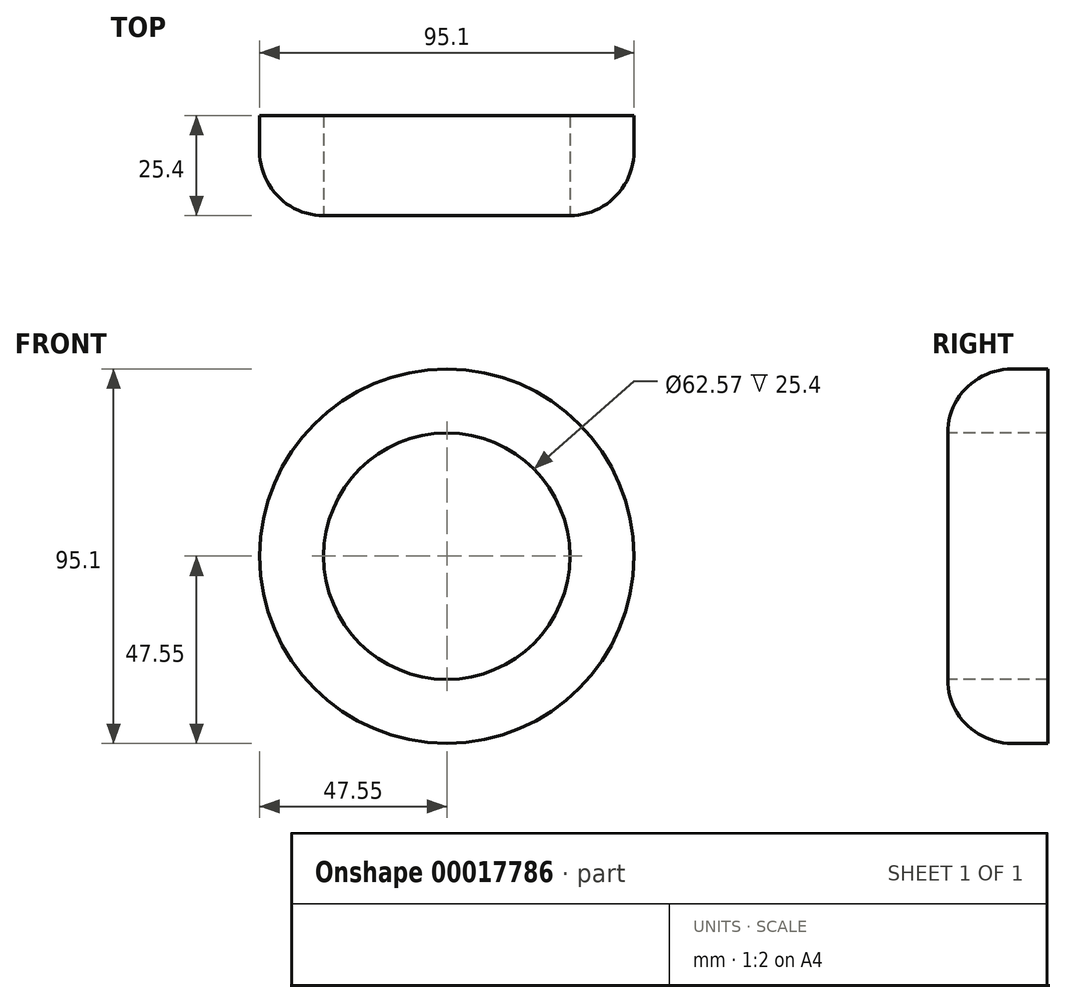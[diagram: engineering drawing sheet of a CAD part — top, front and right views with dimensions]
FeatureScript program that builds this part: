
annotation { "Feature Type Name" : "Feature", "Feature Type Description" : "" }
export const myFeature = defineFeature(function(context is Context, id is Id, definition is map)
    precondition{}
    {
        {
            var Q0;
            Q0=qCreatedBy(makeId("Front.planeOp"),FACE);
            var sketch = newSketch(context, id + "F0", { "sketchPlane" : qUnion([Q0])});
            skCircle(sketch, "E0", {"center": v(0, 0) * mm, "radius": 47.55 * mm});
            skSolve(sketch);
        }
        {
            var Q0;
            Q0 = qSketchRegion(id + "F0", true);
            extrude(context, id + "F1", {"entities" : qUnion([Q0]), "depth" : 25.4 * mm});
        }
        {
            var Q0;
            Q0=makeQuery(id+"F1.opExtrude","CAP_EDGE",EDGE,{"disambiguationData":[OSD([sQuery(id+"F0.wireOp",EDGE,"E0")])],"isStart":false});
            fillet(context, id + "F2", {"entities" : qUnion([Q0]), "radius" : 16.26 * mm, "tangentPropagation" : true, "allowEdgeOverflow" : false});
        }
        {
            var Q0;
            Q0=makeQuery(id+"F1.opExtrude","CAP_FACE",FACE,{"disambiguationData":[OSD([sQuery(id+"F0.wireOp",EDGE,"E0")])],"isStart":false});
            extrude(context, id + "F3", {"entities" : qUnion([Q0]), "operationType" : NewBodyOperationType.REMOVE, "oppositeDirection" : true, "depth" : 25.4 * mm});
        }
    });
